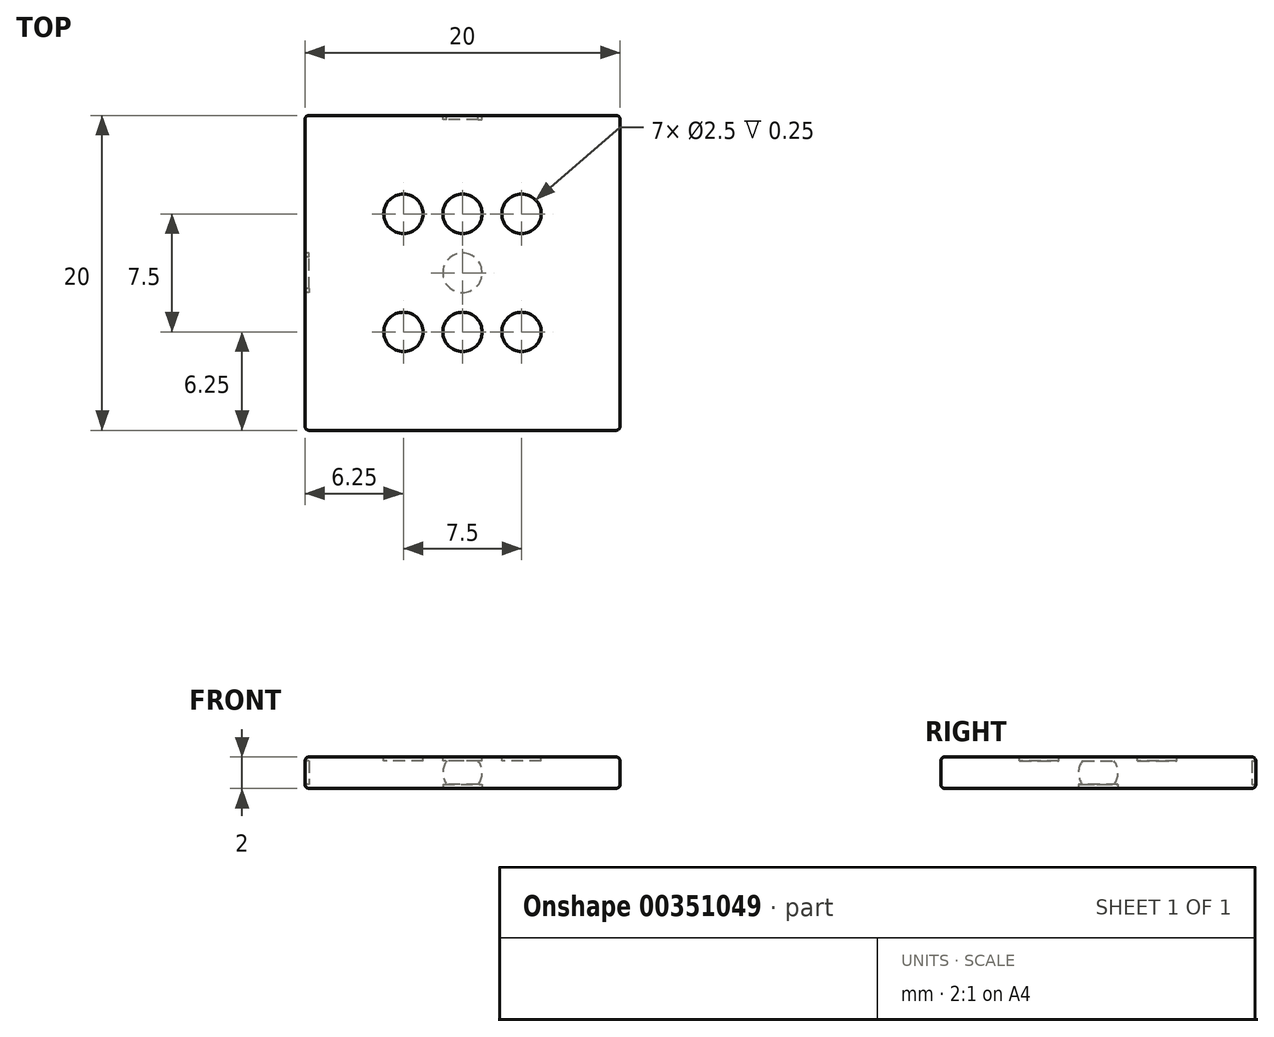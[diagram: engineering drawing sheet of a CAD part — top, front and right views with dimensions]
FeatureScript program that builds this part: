
annotation { "Feature Type Name" : "Feature", "Feature Type Description" : "" }
export const myFeature = defineFeature(function(context is Context, id is Id, definition is map)
    precondition{}
    {
        {
            assignVariable(context, id + "F0", {"name" : "H", "anyValue" : 2});
        }
        {
            assignVariable(context, id + "F1", {"name" : "E", "anyValue" : .25});
        }
        {
            var Q0;
            Q0=qCreatedBy(makeId("Top.planeOp"),FACE);
            var sketch = newSketch(context, id + "F2", { "sketchPlane" : qUnion([Q0])});
            skLineSegment(sketch, "E0.bottom", {"start": v(0, 0) * mm, "end": v(-10, 0) * mm});
            skLineSegment(sketch, "E0.top", {"start": v(0, 10) * mm, "end": v(-10, 10) * mm});
            skLineSegment(sketch, "E0.left", {"start": v(0, 0) * mm, "end": v(0, 10) * mm});
            skLineSegment(sketch, "E0.right", {"start": v(-10, 0) * mm, "end": v(-10, 10) * mm});
            skLineSegment(sketch, "E1.MirrorCS", {"start": v(0, 10) * mm, "end": v(10, 10) * mm});
            skLineSegment(sketch, "E2.MirrorCS", {"start": v(10, 0) * mm, "end": v(10, 10) * mm});
            skLineSegment(sketch, "E3.MirrorCS", {"start": v(0, 0) * mm, "end": v(10, 0) * mm});
            skLineSegment(sketch, "E4.MirrorCS", {"start": v(0, -10) * mm, "end": v(-10, -10) * mm});
            skLineSegment(sketch, "E5.MirrorCS", {"start": v(0, -10) * mm, "end": v(10, -10) * mm});
            skLineSegment(sketch, "E6.MirrorCS", {"start": v(-10, 0) * mm, "end": v(-10, -10) * mm});
            skLineSegment(sketch, "E7.MirrorCS", {"start": v(10, 0) * mm, "end": v(10, -10) * mm});
            skLineSegment(sketch, "E8", {"start": v(10, 0) * mm, "end": v(30, 0) * mm});
            skPoint(sketch, "E9", {"position": v(10, 5) * mm});
            skPoint(sketch, "E10", {"position": v(10, -5) * mm});
            skPoint(sketch, "E11", {"position": v(20, 0) * mm});
            skPoint(sketch, "E12", {"position": v(25, 0) * mm});
            skCircle(sketch, "E13", {"center": v(25, 0) * mm, "radius": 5 * mm});
            skLineSegment(sketch, "E14", {"start": v(25, 0) * mm, "end": v(10, 5) * mm});
            skLineSegment(sketch, "E15", {"start": v(10, -5) * mm, "end": v(25, 0) * mm});
            skLineSegment(sketch, "E16", {"start": v(30, 0) * mm, "end": v(10, 10) * mm});
            skLineSegment(sketch, "E17", {"start": v(30, 0) * mm, "end": v(10, -10) * mm});
            skCircle(sketch, "E18.MirrorC", {"center": v(-25, 0) * mm, "radius": 5 * mm});
            skLineSegment(sketch, "E19.MirrorCS", {"start": v(-25, 0) * mm, "end": v(-10, 5) * mm});
            skLineSegment(sketch, "E20.MirrorCS", {"start": v(-30, 0) * mm, "end": v(-10, 10) * mm});
            skLineSegment(sketch, "E21.MirrorCS", {"start": v(-10, 0) * mm, "end": v(-30, 0) * mm});
            skPoint(sketch, "E22", {"position": v(10, 7.5) * mm});
            skPoint(sketch, "E23", {"position": v(10, -7.5) * mm});
            skPoint(sketch, "E24.oppositeSnap0", {"position": v(17.5, 2.5) * mm});
            skLineSegment(sketch, "E24.bottom", {"start": v(10, 7.5) * mm, "end": v(17.5, 7.5) * mm});
            skLineSegment(sketch, "E24.top", {"start": v(10, -7.5) * mm, "end": v(17.5, -7.5) * mm});
            skLineSegment(sketch, "E24.left", {"start": v(10, 7.5) * mm, "end": v(10, -7.5) * mm});
            skLineSegment(sketch, "E24.right", {"start": v(17.5, 7.5) * mm, "end": v(17.5, -7.5) * mm});
            skLineSegment(sketch, "E25.MirrorCS", {"start": v(-10, 7.5) * mm, "end": v(-17.5, 7.5) * mm});
            skLineSegment(sketch, "E26.MirrorCS", {"start": v(-17.5, 7.5) * mm, "end": v(-17.5, -7.5) * mm});
            skLineSegment(sketch, "E27", {"start": v(13.75, 7.5) * mm, "end": v(13.75, -7.5) * mm});
            skLineSegment(sketch, "E28.MirrorCS", {"start": v(-13.75, 7.5) * mm, "end": v(-13.75, -7.5) * mm});
            skSolve(sketch);
        }
        {
            var Q0;
            Q0=makeQuery(id+"F2.imprint","IMPRINT",FACE,{"disambiguationData":[TD([[makeQuery(id+"F2.imprint","IMPRINT",EDGE,{"derivedFrom":sQuery(id+"F2.wireOp",EDGE,"E0.bottom")}),-1.0]])]});
            var Q1;
            Q1=makeQuery(id+"F2.imprint","IMPRINT",FACE,{"disambiguationData":[TD([[makeQuery(id+"F2.imprint","IMPRINT",EDGE,{"derivedFrom":sQuery(id+"F2.wireOp",EDGE,"E0.left")}),-1.0]])]});
            var Q2;
            Q2=makeQuery(id+"F2.imprint","IMPRINT",FACE,{"disambiguationData":[TD([[makeQuery(id+"F2.imprint","IMPRINT",EDGE,{"derivedFrom":sQuery(id+"F2.wireOp",EDGE,"E0.bottom")}),1.0]])]});
            extrude(context, id + "F3", {"entities" : qUnion([Q0, Q1, Q2]), "depth" : (getVariable(context, 'H') / 2) * mm, "hasSecondDirection" : true, "secondDirectionOppositeDirection" : true, "secondDirectionDepth" : (getVariable(context, 'H') / 2) * mm});
        }
        {
            var Q0;
            Q0=makeQuery(id+"F3.opExtrude","CAP_EDGE",EDGE,{"disambiguationData":[OSD([sQuery(id+"F2.wireOp",EDGE,"E4.MirrorCS"),sQuery(id+"F2.wireOp",EDGE,"E5.MirrorCS")])],"isStart":false});
            var Q1;
            Q1=makeQuery(id+"F3.opExtrude","CAP_EDGE",EDGE,{"disambiguationData":[OSD([sQuery(id+"F2.wireOp",EDGE,"E0.top"),sQuery(id+"F2.wireOp",EDGE,"E1.MirrorCS")])],"isStart":false});
            var Q2;
            Q2=makeQuery(id+"F3.opExtrude","CAP_EDGE",EDGE,{"disambiguationData":[OSD([sQuery(id+"F2.wireOp",EDGE,"E4.MirrorCS"),sQuery(id+"F2.wireOp",EDGE,"E5.MirrorCS")])],"isStart":true});
            var Q3;
            Q3=makeQuery(id+"F3.opExtrude","CAP_EDGE",EDGE,{"disambiguationData":[OSD([sQuery(id+"F2.wireOp",EDGE,"E0.top"),sQuery(id+"F2.wireOp",EDGE,"E1.MirrorCS")])],"isStart":true});
            var Q4;
            Q4=makeQuery(id+"F3.opExtrude","CAP_EDGE",EDGE,{"disambiguationData":[OSD([sQuery(id+"F2.wireOp",EDGE,"E0.right"),sQuery(id+"F2.wireOp",EDGE,"E6.MirrorCS")])],"isStart":true});
            var Q5;
            Q5=makeQuery(id+"F3.opExtrude","SWEPT_EDGE",EDGE,{"disambiguationData":[OSD([sQuery(id+"F2.wireOp",EDGE,"E0.top"),sQuery(id+"F2.wireOp",EDGE,"E0.right")])]});
            var Q6;
            Q6=makeQuery(id+"F3.opExtrude","SWEPT_FACE",FACE,{"disambiguationData":[OSD([sQuery(id+"F2.wireOp",EDGE,"E0.right"),sQuery(id+"F2.wireOp",EDGE,"E6.MirrorCS")])]});
            var Q7;
            Q7=makeQuery(id+"F3.opExtrude","SWEPT_FACE",FACE,{"disambiguationData":[OSD([sQuery(id+"F2.wireOp",EDGE,"E2.MirrorCS"),sQuery(id+"F2.wireOp",EDGE,"E7.MirrorCS")])]});
            fillet(context, id + "F4", {"entities" : qUnion([Q0, Q1, Q2, Q3, Q4, Q5, Q6, Q7]), "radius" : (getVariable(context, 'E')) * mm, "tangentPropagation" : true, "allowEdgeOverflow" : false});
        }
        {
            var Q0;
            Q0=makeQuery(id+"F3.opExtrude","CAP_FACE",FACE,{"disambiguationData":[OSD([sQuery(id+"F2.wireOp",EDGE,"E0.top"),sQuery(id+"F2.wireOp",EDGE,"E0.right"),sQuery(id+"F2.wireOp",EDGE,"E1.MirrorCS"),sQuery(id+"F2.wireOp",EDGE,"E2.MirrorCS"),sQuery(id+"F2.wireOp",EDGE,"E4.MirrorCS"),sQuery(id+"F2.wireOp",EDGE,"E5.MirrorCS"),sQuery(id+"F2.wireOp",EDGE,"E6.MirrorCS"),sQuery(id+"F2.wireOp",EDGE,"E7.MirrorCS")])],"isStart":false});
            var sketch = newSketch(context, id + "F5", { "sketchPlane" : qUnion([Q0])});
            skLineSegment(sketch, "E29.bottom", {"start": v(-3.75, 3.75) * mm, "end": v(3.75, 3.75) * mm});
            skLineSegment(sketch, "E29.top", {"start": v(-3.75, -3.75) * mm, "end": v(3.75, -3.75) * mm});
            skLineSegment(sketch, "E29.left", {"start": v(-3.75, 3.75) * mm, "end": v(-3.75, -3.75) * mm});
            skLineSegment(sketch, "E29.right", {"start": v(3.75, 3.75) * mm, "end": v(3.75, -3.75) * mm});
            skPoint(sketch, "E29.middle", {"position": v(0, 0) * mm});
            skLineSegment(sketch, "E30", {"start": v(-3.75, 0) * mm, "end": v(3.75, 0) * mm});
            skLineSegment(sketch, "E31", {"start": v(0, 3.75) * mm, "end": v(0, -3.75) * mm});
            skCircle(sketch, "E32", {"center": v(-3.75, 0) * mm, "radius": 1.25 * mm});
            skCircle(sketch, "E33", {"center": v(-3.75, 3.75) * mm, "radius": 1.25 * mm});
            skCircle(sketch, "E34", {"center": v(0, 3.75) * mm, "radius": 1.25 * mm});
            skCircle(sketch, "E35", {"center": v(0, 0) * mm, "radius": 1.25 * mm});
            skCircle(sketch, "E36.MirrorC", {"center": v(3.75, 3.75) * mm, "radius": 1.25 * mm});
            skCircle(sketch, "E37.MirrorC", {"center": v(3.75, 0) * mm, "radius": 1.25 * mm});
            skCircle(sketch, "E38.MirrorC", {"center": v(0, -3.75) * mm, "radius": 1.25 * mm});
            skCircle(sketch, "E39.MirrorC", {"center": v(-3.75, -3.75) * mm, "radius": 1.25 * mm});
            skCircle(sketch, "E40.MirrorC", {"center": v(3.75, -3.75) * mm, "radius": 1.25 * mm});
            skSolve(sketch);
        }
        {
            var Q0;
            Q0=makeQuery(id+"F3.opExtrude","CAP_FACE",FACE,{"disambiguationData":[OSD([sQuery(id+"F2.wireOp",EDGE,"E0.top"),sQuery(id+"F2.wireOp",EDGE,"E0.right"),sQuery(id+"F2.wireOp",EDGE,"E1.MirrorCS"),sQuery(id+"F2.wireOp",EDGE,"E2.MirrorCS"),sQuery(id+"F2.wireOp",EDGE,"E4.MirrorCS"),sQuery(id+"F2.wireOp",EDGE,"E5.MirrorCS"),sQuery(id+"F2.wireOp",EDGE,"E6.MirrorCS"),sQuery(id+"F2.wireOp",EDGE,"E7.MirrorCS")])],"isStart":true});
            var sketch = newSketch(context, id + "F6", { "sketchPlane" : qUnion([Q0])});
            skLineSegment(sketch, "E41.bottom", {"start": v(-3.75, 3.75) * mm, "end": v(3.75, 3.75) * mm});
            skLineSegment(sketch, "E41.top", {"start": v(-3.75, -3.75) * mm, "end": v(3.75, -3.75) * mm});
            skLineSegment(sketch, "E41.left", {"start": v(-3.75, 3.75) * mm, "end": v(-3.75, -3.75) * mm});
            skLineSegment(sketch, "E41.right", {"start": v(3.75, 3.75) * mm, "end": v(3.75, -3.75) * mm});
            skPoint(sketch, "E41.middle", {"position": v(0, 0) * mm});
            skLineSegment(sketch, "E42", {"start": v(-3.75, 0) * mm, "end": v(3.75, 0) * mm});
            skLineSegment(sketch, "E43", {"start": v(0, 3.75) * mm, "end": v(0, -3.75) * mm});
            skCircle(sketch, "E44", {"center": v(-3.75, 0) * mm, "radius": 1.25 * mm});
            skCircle(sketch, "E45", {"center": v(-3.75, 3.75) * mm, "radius": 1.25 * mm});
            skCircle(sketch, "E46", {"center": v(0, 3.75) * mm, "radius": 1.25 * mm});
            skCircle(sketch, "E47", {"center": v(0, 0) * mm, "radius": 1.25 * mm});
            skCircle(sketch, "E48.MirrorC", {"center": v(3.75, -3.75) * mm, "radius": 1.25 * mm});
            skCircle(sketch, "E49.MirrorC", {"center": v(3.75, 0) * mm, "radius": 1.25 * mm});
            skCircle(sketch, "E50.MirrorC", {"center": v(0, -3.75) * mm, "radius": 1.25 * mm});
            skCircle(sketch, "E51.MirrorC", {"center": v(-3.75, -3.75) * mm, "radius": 1.25 * mm});
            skCircle(sketch, "E52.MirrorC", {"center": v(3.75, 3.75) * mm, "radius": 1.25 * mm});
            skSolve(sketch);
        }
        {
            var Q0;
            Q0=makeQuery(id+"F3.opExtrude","SWEPT_FACE",FACE,{"disambiguationData":[OSD([sQuery(id+"F2.wireOp",EDGE,"E4.MirrorCS"),sQuery(id+"F2.wireOp",EDGE,"E5.MirrorCS")])]});
            var sketch = newSketch(context, id + "F7", { "sketchPlane" : qUnion([Q0])});
            skLineSegment(sketch, "E53.bottom", {"start": v(-3.75, 3.75) * mm, "end": v(3.75, 3.75) * mm});
            skLineSegment(sketch, "E53.top", {"start": v(-3.75, -3.75) * mm, "end": v(3.75, -3.75) * mm});
            skLineSegment(sketch, "E53.left", {"start": v(-3.75, 3.75) * mm, "end": v(-3.75, -3.75) * mm});
            skLineSegment(sketch, "E53.right", {"start": v(3.75, 3.75) * mm, "end": v(3.75, -3.75) * mm});
            skPoint(sketch, "E53.middle", {"position": v(0, 0) * mm});
            skLineSegment(sketch, "E54", {"start": v(-3.75, 0) * mm, "end": v(3.75, 0) * mm});
            skLineSegment(sketch, "E55", {"start": v(0, 3.75) * mm, "end": v(0, -3.75) * mm});
            skCircle(sketch, "E56", {"center": v(-3.75, 0) * mm, "radius": 1.25 * mm});
            skCircle(sketch, "E57", {"center": v(-3.75, 3.75) * mm, "radius": 1.25 * mm});
            skCircle(sketch, "E58", {"center": v(0, 3.75) * mm, "radius": 1.25 * mm});
            skCircle(sketch, "E59", {"center": v(0, 0) * mm, "radius": 1.25 * mm});
            skCircle(sketch, "E60.MirrorC", {"center": v(3.75, 3.75) * mm, "radius": 1.25 * mm});
            skCircle(sketch, "E61.MirrorC", {"center": v(3.75, 0) * mm, "radius": 1.25 * mm});
            skCircle(sketch, "E62.MirrorC", {"center": v(0, -3.75) * mm, "radius": 1.25 * mm});
            skCircle(sketch, "E63.MirrorC", {"center": v(-3.75, -3.75) * mm, "radius": 1.25 * mm});
            skCircle(sketch, "E64.MirrorC", {"center": v(3.75, -3.75) * mm, "radius": 1.25 * mm});
            skSolve(sketch);
        }
        {
            var Q0;
            Q0=makeQuery(id+"F3.opExtrude","SWEPT_FACE",FACE,{"disambiguationData":[OSD([sQuery(id+"F2.wireOp",EDGE,"E0.top"),sQuery(id+"F2.wireOp",EDGE,"E1.MirrorCS")])]});
            var sketch = newSketch(context, id + "F8", { "sketchPlane" : qUnion([Q0])});
            skLineSegment(sketch, "E65.bottom", {"start": v(-3.75, 3.75) * mm, "end": v(3.75, 3.75) * mm});
            skLineSegment(sketch, "E65.top", {"start": v(-3.75, -3.75) * mm, "end": v(3.75, -3.75) * mm});
            skLineSegment(sketch, "E65.left", {"start": v(-3.75, 3.75) * mm, "end": v(-3.75, -3.75) * mm});
            skLineSegment(sketch, "E65.right", {"start": v(3.75, 3.75) * mm, "end": v(3.75, -3.75) * mm});
            skPoint(sketch, "E65.middle", {"position": v(0, 0) * mm});
            skLineSegment(sketch, "E66", {"start": v(-3.75, 0) * mm, "end": v(3.75, 0) * mm});
            skLineSegment(sketch, "E67", {"start": v(0, 3.75) * mm, "end": v(0, -3.75) * mm});
            skCircle(sketch, "E68", {"center": v(-3.75, 0) * mm, "radius": 1.25 * mm});
            skCircle(sketch, "E69", {"center": v(-3.75, 3.75) * mm, "radius": 1.25 * mm});
            skCircle(sketch, "E70", {"center": v(0, 3.75) * mm, "radius": 1.25 * mm});
            skCircle(sketch, "E71", {"center": v(0, 0) * mm, "radius": 1.25 * mm});
            skCircle(sketch, "E72.MirrorC", {"center": v(3.75, -3.75) * mm, "radius": 1.25 * mm});
            skCircle(sketch, "E73.MirrorC", {"center": v(3.75, 0) * mm, "radius": 1.25 * mm});
            skCircle(sketch, "E74.MirrorC", {"center": v(0, -3.75) * mm, "radius": 1.25 * mm});
            skCircle(sketch, "E75.MirrorC", {"center": v(-3.75, -3.75) * mm, "radius": 1.25 * mm});
            skCircle(sketch, "E76.MirrorC", {"center": v(3.75, 3.75) * mm, "radius": 1.25 * mm});
            skSolve(sketch);
        }
        {
            var Q0;
            Q0=makeQuery(id+"F3.opExtrude","SWEPT_FACE",FACE,{"disambiguationData":[OSD([sQuery(id+"F2.wireOp",EDGE,"E2.MirrorCS"),sQuery(id+"F2.wireOp",EDGE,"E7.MirrorCS"),sQuery(id+"F2.wireOp",EDGE,"E24.left")])]});
            var sketch = newSketch(context, id + "F9", { "sketchPlane" : qUnion([Q0])});
            skLineSegment(sketch, "E77.bottom", {"start": v(-3.75, 3.75) * mm, "end": v(3.75, 3.75) * mm});
            skLineSegment(sketch, "E77.top", {"start": v(-3.75, -3.75) * mm, "end": v(3.75, -3.75) * mm});
            skLineSegment(sketch, "E77.left", {"start": v(-3.75, 3.75) * mm, "end": v(-3.75, -3.75) * mm});
            skLineSegment(sketch, "E77.right", {"start": v(3.75, 3.75) * mm, "end": v(3.75, -3.75) * mm});
            skPoint(sketch, "E77.middle", {"position": v(0, 0) * mm});
            skLineSegment(sketch, "E78", {"start": v(-3.75, 0) * mm, "end": v(3.75, 0) * mm});
            skLineSegment(sketch, "E79", {"start": v(0, 3.75) * mm, "end": v(0, -3.75) * mm});
            skCircle(sketch, "E80", {"center": v(-3.75, 0) * mm, "radius": 1.25 * mm});
            skCircle(sketch, "E81", {"center": v(-3.75, 3.75) * mm, "radius": 1.25 * mm});
            skCircle(sketch, "E82", {"center": v(0, 3.75) * mm, "radius": 1.25 * mm});
            skCircle(sketch, "E83", {"center": v(0, 0) * mm, "radius": 1.25 * mm});
            skCircle(sketch, "E84.MirrorC", {"center": v(3.75, -3.75) * mm, "radius": 1.25 * mm});
            skCircle(sketch, "E85.MirrorC", {"center": v(3.75, 0) * mm, "radius": 1.25 * mm});
            skCircle(sketch, "E86.MirrorC", {"center": v(0, -3.75) * mm, "radius": 1.25 * mm});
            skCircle(sketch, "E87.MirrorC", {"center": v(-3.75, -3.75) * mm, "radius": 1.25 * mm});
            skCircle(sketch, "E88.MirrorC", {"center": v(3.75, 3.75) * mm, "radius": 1.25 * mm});
            skSolve(sketch);
        }
        {
            var Q0;
            Q0=makeQuery(id+"F3.opExtrude","SWEPT_FACE",FACE,{"disambiguationData":[OSD([sQuery(id+"F2.wireOp",EDGE,"E0.right"),sQuery(id+"F2.wireOp",EDGE,"E6.MirrorCS")])]});
            var sketch = newSketch(context, id + "F10", { "sketchPlane" : qUnion([Q0])});
            skLineSegment(sketch, "E89.bottom", {"start": v(-3.75, 3.75) * mm, "end": v(3.75, 3.75) * mm});
            skLineSegment(sketch, "E89.top", {"start": v(-3.75, -3.75) * mm, "end": v(3.75, -3.75) * mm});
            skLineSegment(sketch, "E89.left", {"start": v(-3.75, 3.75) * mm, "end": v(-3.75, -3.75) * mm});
            skLineSegment(sketch, "E89.right", {"start": v(3.75, 3.75) * mm, "end": v(3.75, -3.75) * mm});
            skPoint(sketch, "E89.middle", {"position": v(0, 0) * mm});
            skLineSegment(sketch, "E90", {"start": v(-3.75, 0) * mm, "end": v(3.75, 0) * mm});
            skLineSegment(sketch, "E91", {"start": v(0, 3.75) * mm, "end": v(0, -3.75) * mm});
            skCircle(sketch, "E92", {"center": v(-3.75, 0) * mm, "radius": 1.25 * mm});
            skCircle(sketch, "E93", {"center": v(-3.75, 3.75) * mm, "radius": 1.25 * mm});
            skCircle(sketch, "E94", {"center": v(0, 3.75) * mm, "radius": 1.25 * mm});
            skCircle(sketch, "E95", {"center": v(0, 0) * mm, "radius": 1.25 * mm});
            skCircle(sketch, "E96.MirrorC", {"center": v(3.75, -3.75) * mm, "radius": 1.25 * mm});
            skCircle(sketch, "E97.MirrorC", {"center": v(3.75, 0) * mm, "radius": 1.25 * mm});
            skCircle(sketch, "E98.MirrorC", {"center": v(0, -3.75) * mm, "radius": 1.25 * mm});
            skCircle(sketch, "E99.MirrorC", {"center": v(-3.75, -3.75) * mm, "radius": 1.25 * mm});
            skCircle(sketch, "E100.MirrorC", {"center": v(3.75, 3.75) * mm, "radius": 1.25 * mm});
            skSolve(sketch);
        }
        {
            var Q0;
            {var subQ0=sQuery(id+"F5.wireOp",EDGE,"E29.bottom");var subQ1=makeQuery(id+"F5.imprint","INTERSECT",VERTEX,{"derivedFrom":[subQ0,sQuery(id+"F5.wireOp",EDGE,"E31")]});Q0=makeQuery(id+"F5.imprint","IMPRINT",FACE,{"disambiguationData":[TD([[makeQuery(id+"F5.imprint","IMPRINT",EDGE,{"disambiguationData":[TD([[subQ1,1.0]])],"derivedFrom":subQ0}),1.0]])]});}
            var Q1;
            {var subQ0=sQuery(id+"F5.wireOp",EDGE,"E31");var subQ1=sQuery(id+"F5.wireOp",EDGE,"E29.bottom");var subQ2=makeQuery(id+"F5.imprint","INTERSECT",VERTEX,{"derivedFrom":[subQ1,subQ0]});Q1=makeQuery(id+"F5.imprint","IMPRINT",FACE,{"disambiguationData":[TD([[makeQuery(id+"F5.imprint","IMPRINT",EDGE,{"disambiguationData":[TD([[subQ2,-1.0]])],"derivedFrom":subQ1}),-1.0]])]});}
            var Q2;
            {var subQ0=sQuery(id+"F5.wireOp",EDGE,"E31");var subQ1=sQuery(id+"F5.wireOp",EDGE,"E29.bottom");var subQ2=makeQuery(id+"F5.imprint","INTERSECT",VERTEX,{"derivedFrom":[subQ1,subQ0]});Q2=makeQuery(id+"F5.imprint","IMPRINT",FACE,{"disambiguationData":[TD([[makeQuery(id+"F5.imprint","IMPRINT",EDGE,{"disambiguationData":[TD([[subQ2,1.0]])],"derivedFrom":subQ1}),-1.0]])]});}
            var Q3;
            {var subQ0=sQuery(id+"F5.wireOp",EDGE,"E31");var subQ1=sQuery(id+"F5.wireOp",EDGE,"E29.top");var subQ2=makeQuery(id+"F5.imprint","INTERSECT",VERTEX,{"derivedFrom":[subQ1,subQ0]});Q3=makeQuery(id+"F5.imprint","IMPRINT",FACE,{"disambiguationData":[TD([[makeQuery(id+"F5.imprint","IMPRINT",EDGE,{"disambiguationData":[TD([[subQ2,-1.0]])],"derivedFrom":subQ1}),1.0]])]});}
            var Q4;
            {var subQ0=sQuery(id+"F5.wireOp",EDGE,"E31");var subQ1=sQuery(id+"F5.wireOp",EDGE,"E29.top");var subQ2=makeQuery(id+"F5.imprint","INTERSECT",VERTEX,{"derivedFrom":[subQ1,subQ0]});Q4=makeQuery(id+"F5.imprint","IMPRINT",FACE,{"disambiguationData":[TD([[makeQuery(id+"F5.imprint","IMPRINT",EDGE,{"disambiguationData":[TD([[subQ2,1.0]])],"derivedFrom":subQ1}),1.0]])]});}
            var Q5;
            {var subQ0=sQuery(id+"F5.wireOp",EDGE,"E29.top");var subQ1=makeQuery(id+"F5.imprint","INTERSECT",VERTEX,{"derivedFrom":[subQ0,sQuery(id+"F5.wireOp",EDGE,"E31")]});Q5=makeQuery(id+"F5.imprint","IMPRINT",FACE,{"disambiguationData":[TD([[makeQuery(id+"F5.imprint","IMPRINT",EDGE,{"disambiguationData":[TD([[subQ1,1.0]])],"derivedFrom":subQ0}),-1.0]])]});}
            var Q6;
            {var subQ0=sQuery(id+"F5.wireOp",EDGE,"E29.right");var subQ1=sQuery(id+"F5.wireOp",EDGE,"E29.bottom");var subQ2=makeQuery(id+"F5.imprint","INTERSECT",VERTEX,{"derivedFrom":[subQ1,subQ0]});Q6=makeQuery(id+"F5.imprint","IMPRINT",FACE,{"disambiguationData":[TD([[makeQuery(id+"F5.imprint","IMPRINT",EDGE,{"disambiguationData":[TD([[subQ2,1.0]])],"derivedFrom":subQ1}),1.0]])]});}
            var Q7;
            {var subQ0=sQuery(id+"F5.wireOp",EDGE,"E29.right");var subQ1=sQuery(id+"F5.wireOp",EDGE,"E29.top");var subQ2=makeQuery(id+"F5.imprint","INTERSECT",VERTEX,{"derivedFrom":[subQ1,subQ0]});Q7=makeQuery(id+"F5.imprint","IMPRINT",FACE,{"disambiguationData":[TD([[makeQuery(id+"F5.imprint","IMPRINT",EDGE,{"disambiguationData":[TD([[subQ2,1.0]])],"derivedFrom":subQ1}),-1.0]])]});}
            var Q8;
            {var subQ0=sQuery(id+"F5.wireOp",EDGE,"E29.right");var subQ1=sQuery(id+"F5.wireOp",EDGE,"E29.top");var subQ2=makeQuery(id+"F5.imprint","INTERSECT",VERTEX,{"derivedFrom":[subQ1,subQ0]});Q8=makeQuery(id+"F5.imprint","IMPRINT",FACE,{"disambiguationData":[TD([[makeQuery(id+"F5.imprint","IMPRINT",EDGE,{"disambiguationData":[TD([[subQ2,1.0]])],"derivedFrom":subQ1}),1.0]])]});}
            var Q9;
            {var subQ0=sQuery(id+"F5.wireOp",EDGE,"E29.right");var subQ1=sQuery(id+"F5.wireOp",EDGE,"E29.bottom");var subQ2=makeQuery(id+"F5.imprint","INTERSECT",VERTEX,{"derivedFrom":[subQ1,subQ0]});Q9=makeQuery(id+"F5.imprint","IMPRINT",FACE,{"disambiguationData":[TD([[makeQuery(id+"F5.imprint","IMPRINT",EDGE,{"disambiguationData":[TD([[subQ2,1.0]])],"derivedFrom":subQ1}),-1.0]])]});}
            var Q10;
            {var subQ0=sQuery(id+"F5.wireOp",EDGE,"E29.left");var subQ1=sQuery(id+"F5.wireOp",EDGE,"E29.top");var subQ2=makeQuery(id+"F5.imprint","INTERSECT",VERTEX,{"derivedFrom":[subQ1,subQ0]});Q10=makeQuery(id+"F5.imprint","IMPRINT",FACE,{"disambiguationData":[TD([[makeQuery(id+"F5.imprint","IMPRINT",EDGE,{"disambiguationData":[TD([[subQ2,-1.0]])],"derivedFrom":subQ1}),-1.0]])]});}
            var Q11;
            {var subQ0=sQuery(id+"F5.wireOp",EDGE,"E29.left");var subQ1=sQuery(id+"F5.wireOp",EDGE,"E29.top");var subQ2=makeQuery(id+"F5.imprint","INTERSECT",VERTEX,{"derivedFrom":[subQ1,subQ0]});Q11=makeQuery(id+"F5.imprint","IMPRINT",FACE,{"disambiguationData":[TD([[makeQuery(id+"F5.imprint","IMPRINT",EDGE,{"disambiguationData":[TD([[subQ2,-1.0]])],"derivedFrom":subQ1}),1.0]])]});}
            var Q12;
            {var subQ0=sQuery(id+"F5.wireOp",EDGE,"E29.left");var subQ1=sQuery(id+"F5.wireOp",EDGE,"E29.bottom");var subQ2=makeQuery(id+"F5.imprint","INTERSECT",VERTEX,{"derivedFrom":[subQ1,subQ0]});Q12=makeQuery(id+"F5.imprint","IMPRINT",FACE,{"disambiguationData":[TD([[makeQuery(id+"F5.imprint","IMPRINT",EDGE,{"disambiguationData":[TD([[subQ2,-1.0]])],"derivedFrom":subQ1}),1.0]])]});}
            var Q13;
            {var subQ0=sQuery(id+"F5.wireOp",EDGE,"E29.left");var subQ1=sQuery(id+"F5.wireOp",EDGE,"E29.bottom");var subQ2=makeQuery(id+"F5.imprint","INTERSECT",VERTEX,{"derivedFrom":[subQ1,subQ0]});Q13=makeQuery(id+"F5.imprint","IMPRINT",FACE,{"disambiguationData":[TD([[makeQuery(id+"F5.imprint","IMPRINT",EDGE,{"disambiguationData":[TD([[subQ2,-1.0]])],"derivedFrom":subQ1}),-1.0]])]});}
            extrude(context, id + "F11", {"entities" : qUnion([Q0, Q1, Q2, Q3, Q4, Q5, Q6, Q7, Q8, Q9, Q10, Q11, Q12, Q13]), "operationType" : NewBodyOperationType.REMOVE, "oppositeDirection" : true, "depth" : (getVariable(context, 'E')) * mm});
        }
        {
            var Q0;
            {var subQ0=sQuery(id+"F6.wireOp",EDGE,"E47");var subQ1=sQuery(id+"F6.wireOp",EDGE,"E42");var subQ2=makeQuery(id+"F6.imprint","INTERSECT",VERTEX,{"disambiguationData":[OD(0.0)],"derivedFrom":[subQ1,subQ0]});Q0=makeQuery(id+"F6.imprint","IMPRINT",FACE,{"disambiguationData":[TD([[makeQuery(id+"F6.imprint","IMPRINT",EDGE,{"disambiguationData":[TD([[subQ2,-1.0]])],"derivedFrom":subQ1}),1.0]])]});}
            var Q1;
            {var subQ0=sQuery(id+"F6.wireOp",EDGE,"E47");var subQ1=sQuery(id+"F6.wireOp",EDGE,"E42");var subQ2=makeQuery(id+"F6.imprint","INTERSECT",VERTEX,{"disambiguationData":[OD(0.0)],"derivedFrom":[subQ1,subQ0]});Q1=makeQuery(id+"F6.imprint","IMPRINT",FACE,{"disambiguationData":[TD([[makeQuery(id+"F6.imprint","IMPRINT",EDGE,{"disambiguationData":[TD([[subQ2,-1.0]])],"derivedFrom":subQ1}),-1.0]])]});}
            var Q2;
            {var subQ0=sQuery(id+"F6.wireOp",EDGE,"E43");var subQ1=sQuery(id+"F6.wireOp",EDGE,"E42");var subQ2=makeQuery(id+"F6.imprint","INTERSECT",VERTEX,{"derivedFrom":[subQ1,subQ0]});Q2=makeQuery(id+"F6.imprint","IMPRINT",FACE,{"disambiguationData":[TD([[makeQuery(id+"F6.imprint","IMPRINT",EDGE,{"disambiguationData":[TD([[subQ2,-1.0]])],"derivedFrom":subQ1}),-1.0]])]});}
            var Q3;
            {var subQ0=sQuery(id+"F6.wireOp",EDGE,"E43");var subQ1=sQuery(id+"F6.wireOp",EDGE,"E42");var subQ2=makeQuery(id+"F6.imprint","INTERSECT",VERTEX,{"derivedFrom":[subQ1,subQ0]});Q3=makeQuery(id+"F6.imprint","IMPRINT",FACE,{"disambiguationData":[TD([[makeQuery(id+"F6.imprint","IMPRINT",EDGE,{"disambiguationData":[TD([[subQ2,-1.0]])],"derivedFrom":subQ1}),1.0]])]});}
            extrude(context, id + "F12", {"entities" : qUnion([Q0, Q1, Q2, Q3]), "operationType" : NewBodyOperationType.REMOVE, "oppositeDirection" : true, "depth" : (getVariable(context, 'E')) * mm});
        }
        {
            var Q0;
            {var subQ0=sQuery(id+"F7.wireOp",EDGE,"E53.right");var subQ1=sQuery(id+"F7.wireOp",EDGE,"E53.top");var subQ2=makeQuery(id+"F7.imprint","INTERSECT",VERTEX,{"derivedFrom":[subQ1,subQ0]});Q0=makeQuery(id+"F7.imprint","IMPRINT",FACE,{"disambiguationData":[TD([[makeQuery(id+"F7.imprint","IMPRINT",EDGE,{"disambiguationData":[TD([[subQ2,1.0]])],"derivedFrom":subQ1}),-1.0]])]});}
            var Q1;
            {var subQ0=sQuery(id+"F7.wireOp",EDGE,"E53.right");var subQ1=sQuery(id+"F7.wireOp",EDGE,"E53.top");var subQ2=makeQuery(id+"F7.imprint","INTERSECT",VERTEX,{"derivedFrom":[subQ1,subQ0]});Q1=makeQuery(id+"F7.imprint","IMPRINT",FACE,{"disambiguationData":[TD([[makeQuery(id+"F7.imprint","IMPRINT",EDGE,{"disambiguationData":[TD([[subQ2,1.0]])],"derivedFrom":subQ1}),1.0]])]});}
            var Q2;
            {var subQ0=sQuery(id+"F7.wireOp",EDGE,"E53.right");var subQ1=sQuery(id+"F7.wireOp",EDGE,"E53.bottom");var subQ2=makeQuery(id+"F7.imprint","INTERSECT",VERTEX,{"derivedFrom":[subQ1,subQ0]});Q2=makeQuery(id+"F7.imprint","IMPRINT",FACE,{"disambiguationData":[TD([[makeQuery(id+"F7.imprint","IMPRINT",EDGE,{"disambiguationData":[TD([[subQ2,1.0]])],"derivedFrom":subQ1}),1.0]])]});}
            var Q3;
            {var subQ0=sQuery(id+"F7.wireOp",EDGE,"E53.right");var subQ1=sQuery(id+"F7.wireOp",EDGE,"E53.bottom");var subQ2=makeQuery(id+"F7.imprint","INTERSECT",VERTEX,{"derivedFrom":[subQ1,subQ0]});Q3=makeQuery(id+"F7.imprint","IMPRINT",FACE,{"disambiguationData":[TD([[makeQuery(id+"F7.imprint","IMPRINT",EDGE,{"disambiguationData":[TD([[subQ2,1.0]])],"derivedFrom":subQ1}),-1.0]])]});}
            var Q4;
            {var subQ0=sQuery(id+"F7.wireOp",EDGE,"E53.left");var subQ1=sQuery(id+"F7.wireOp",EDGE,"E53.top");var subQ2=makeQuery(id+"F7.imprint","INTERSECT",VERTEX,{"derivedFrom":[subQ1,subQ0]});Q4=makeQuery(id+"F7.imprint","IMPRINT",FACE,{"disambiguationData":[TD([[makeQuery(id+"F7.imprint","IMPRINT",EDGE,{"disambiguationData":[TD([[subQ2,-1.0]])],"derivedFrom":subQ1}),-1.0]])]});}
            var Q5;
            {var subQ0=sQuery(id+"F7.wireOp",EDGE,"E53.left");var subQ1=sQuery(id+"F7.wireOp",EDGE,"E53.bottom");var subQ2=makeQuery(id+"F7.imprint","INTERSECT",VERTEX,{"derivedFrom":[subQ1,subQ0]});Q5=makeQuery(id+"F7.imprint","IMPRINT",FACE,{"disambiguationData":[TD([[makeQuery(id+"F7.imprint","IMPRINT",EDGE,{"disambiguationData":[TD([[subQ2,-1.0]])],"derivedFrom":subQ1}),1.0]])]});}
            var Q6;
            {var subQ0=sQuery(id+"F7.wireOp",EDGE,"E53.left");var subQ1=sQuery(id+"F7.wireOp",EDGE,"E53.bottom");var subQ2=makeQuery(id+"F7.imprint","INTERSECT",VERTEX,{"derivedFrom":[subQ1,subQ0]});Q6=makeQuery(id+"F7.imprint","IMPRINT",FACE,{"disambiguationData":[TD([[makeQuery(id+"F7.imprint","IMPRINT",EDGE,{"disambiguationData":[TD([[subQ2,-1.0]])],"derivedFrom":subQ1}),-1.0]])]});}
            var Q7;
            {var subQ0=sQuery(id+"F7.wireOp",EDGE,"E53.left");var subQ1=sQuery(id+"F7.wireOp",EDGE,"E53.top");var subQ2=makeQuery(id+"F7.imprint","INTERSECT",VERTEX,{"derivedFrom":[subQ1,subQ0]});Q7=makeQuery(id+"F7.imprint","IMPRINT",FACE,{"disambiguationData":[TD([[makeQuery(id+"F7.imprint","IMPRINT",EDGE,{"disambiguationData":[TD([[subQ2,-1.0]])],"derivedFrom":subQ1}),1.0]])]});}
            extrude(context, id + "F13", {"entities" : qUnion([Q0, Q1, Q2, Q3, Q4, Q5, Q6, Q7]), "operationType" : NewBodyOperationType.REMOVE, "oppositeDirection" : true, "depth" : (getVariable(context, 'E')) * mm});
        }
        {
            var Q0;
            {var subQ0=sQuery(id+"F8.wireOp",EDGE,"E65.right");var subQ1=sQuery(id+"F8.wireOp",EDGE,"E65.top");var subQ2=makeQuery(id+"F8.imprint","INTERSECT",VERTEX,{"derivedFrom":[subQ1,subQ0]});Q0=makeQuery(id+"F8.imprint","IMPRINT",FACE,{"disambiguationData":[TD([[makeQuery(id+"F8.imprint","IMPRINT",EDGE,{"disambiguationData":[TD([[subQ2,1.0]])],"derivedFrom":subQ1}),-1.0]])]});}
            var Q1;
            {var subQ0=sQuery(id+"F8.wireOp",EDGE,"E65.right");var subQ1=sQuery(id+"F8.wireOp",EDGE,"E65.top");var subQ2=makeQuery(id+"F8.imprint","INTERSECT",VERTEX,{"derivedFrom":[subQ1,subQ0]});Q1=makeQuery(id+"F8.imprint","IMPRINT",FACE,{"disambiguationData":[TD([[makeQuery(id+"F8.imprint","IMPRINT",EDGE,{"disambiguationData":[TD([[subQ2,1.0]])],"derivedFrom":subQ1}),1.0]])]});}
            var Q2;
            {var subQ0=sQuery(id+"F8.wireOp",EDGE,"E71");var subQ1=sQuery(id+"F8.wireOp",EDGE,"E66");var subQ2=makeQuery(id+"F8.imprint","INTERSECT",VERTEX,{"disambiguationData":[OD(0.0)],"derivedFrom":[subQ1,subQ0]});Q2=makeQuery(id+"F8.imprint","IMPRINT",FACE,{"disambiguationData":[TD([[makeQuery(id+"F8.imprint","IMPRINT",EDGE,{"disambiguationData":[TD([[subQ2,-1.0]])],"derivedFrom":subQ1}),1.0]])]});}
            var Q3;
            {var subQ0=sQuery(id+"F8.wireOp",EDGE,"E71");var subQ1=sQuery(id+"F8.wireOp",EDGE,"E66");var subQ2=makeQuery(id+"F8.imprint","INTERSECT",VERTEX,{"disambiguationData":[OD(0.0)],"derivedFrom":[subQ1,subQ0]});Q3=makeQuery(id+"F8.imprint","IMPRINT",FACE,{"disambiguationData":[TD([[makeQuery(id+"F8.imprint","IMPRINT",EDGE,{"disambiguationData":[TD([[subQ2,-1.0]])],"derivedFrom":subQ1}),-1.0]])]});}
            var Q4;
            {var subQ0=sQuery(id+"F8.wireOp",EDGE,"E67");var subQ1=sQuery(id+"F8.wireOp",EDGE,"E66");var subQ2=makeQuery(id+"F8.imprint","INTERSECT",VERTEX,{"derivedFrom":[subQ1,subQ0]});Q4=makeQuery(id+"F8.imprint","IMPRINT",FACE,{"disambiguationData":[TD([[makeQuery(id+"F8.imprint","IMPRINT",EDGE,{"disambiguationData":[TD([[subQ2,-1.0]])],"derivedFrom":subQ1}),-1.0]])]});}
            var Q5;
            {var subQ0=sQuery(id+"F8.wireOp",EDGE,"E67");var subQ1=sQuery(id+"F8.wireOp",EDGE,"E66");var subQ2=makeQuery(id+"F8.imprint","INTERSECT",VERTEX,{"derivedFrom":[subQ1,subQ0]});Q5=makeQuery(id+"F8.imprint","IMPRINT",FACE,{"disambiguationData":[TD([[makeQuery(id+"F8.imprint","IMPRINT",EDGE,{"disambiguationData":[TD([[subQ2,-1.0]])],"derivedFrom":subQ1}),1.0]])]});}
            var Q6;
            {var subQ0=sQuery(id+"F8.wireOp",EDGE,"E65.left");var subQ1=sQuery(id+"F8.wireOp",EDGE,"E65.bottom");var subQ2=makeQuery(id+"F8.imprint","INTERSECT",VERTEX,{"derivedFrom":[subQ1,subQ0]});Q6=makeQuery(id+"F8.imprint","IMPRINT",FACE,{"disambiguationData":[TD([[makeQuery(id+"F8.imprint","IMPRINT",EDGE,{"disambiguationData":[TD([[subQ2,-1.0]])],"derivedFrom":subQ1}),-1.0]])]});}
            var Q7;
            {var subQ0=sQuery(id+"F8.wireOp",EDGE,"E65.left");var subQ1=sQuery(id+"F8.wireOp",EDGE,"E65.bottom");var subQ2=makeQuery(id+"F8.imprint","INTERSECT",VERTEX,{"derivedFrom":[subQ1,subQ0]});Q7=makeQuery(id+"F8.imprint","IMPRINT",FACE,{"disambiguationData":[TD([[makeQuery(id+"F8.imprint","IMPRINT",EDGE,{"disambiguationData":[TD([[subQ2,-1.0]])],"derivedFrom":subQ1}),1.0]])]});}
            extrude(context, id + "F14", {"entities" : qUnion([Q0, Q1, Q2, Q3, Q4, Q5, Q6, Q7]), "operationType" : NewBodyOperationType.REMOVE, "oppositeDirection" : true, "depth" : (getVariable(context, 'E')) * mm});
        }
        {
            var Q0;
            {var subQ0=sQuery(id+"F10.wireOp",EDGE,"E89.left");var subQ1=sQuery(id+"F10.wireOp",EDGE,"E89.bottom");var subQ2=makeQuery(id+"F10.imprint","INTERSECT",VERTEX,{"derivedFrom":[subQ1,subQ0]});Q0=makeQuery(id+"F10.imprint","IMPRINT",FACE,{"disambiguationData":[TD([[makeQuery(id+"F10.imprint","IMPRINT",EDGE,{"disambiguationData":[TD([[subQ2,-1.0]])],"derivedFrom":subQ1}),1.0]])]});}
            var Q1;
            {var subQ0=sQuery(id+"F10.wireOp",EDGE,"E89.left");var subQ1=sQuery(id+"F10.wireOp",EDGE,"E89.bottom");var subQ2=makeQuery(id+"F10.imprint","INTERSECT",VERTEX,{"derivedFrom":[subQ1,subQ0]});Q1=makeQuery(id+"F10.imprint","IMPRINT",FACE,{"disambiguationData":[TD([[makeQuery(id+"F10.imprint","IMPRINT",EDGE,{"disambiguationData":[TD([[subQ2,-1.0]])],"derivedFrom":subQ1}),-1.0]])]});}
            var Q2;
            {var subQ0=sQuery(id+"F10.wireOp",EDGE,"E89.right");var subQ1=sQuery(id+"F10.wireOp",EDGE,"E89.bottom");var subQ2=makeQuery(id+"F10.imprint","INTERSECT",VERTEX,{"derivedFrom":[subQ1,subQ0]});Q2=makeQuery(id+"F10.imprint","IMPRINT",FACE,{"disambiguationData":[TD([[makeQuery(id+"F10.imprint","IMPRINT",EDGE,{"disambiguationData":[TD([[subQ2,1.0]])],"derivedFrom":subQ1}),1.0]])]});}
            var Q3;
            {var subQ0=sQuery(id+"F10.wireOp",EDGE,"E89.right");var subQ1=sQuery(id+"F10.wireOp",EDGE,"E89.bottom");var subQ2=makeQuery(id+"F10.imprint","INTERSECT",VERTEX,{"derivedFrom":[subQ1,subQ0]});Q3=makeQuery(id+"F10.imprint","IMPRINT",FACE,{"disambiguationData":[TD([[makeQuery(id+"F10.imprint","IMPRINT",EDGE,{"disambiguationData":[TD([[subQ2,1.0]])],"derivedFrom":subQ1}),-1.0]])]});}
            var Q4;
            {var subQ0=sQuery(id+"F10.wireOp",EDGE,"E91");var subQ1=sQuery(id+"F10.wireOp",EDGE,"E90");var subQ2=makeQuery(id+"F10.imprint","INTERSECT",VERTEX,{"derivedFrom":[subQ1,subQ0]});Q4=makeQuery(id+"F10.imprint","IMPRINT",FACE,{"disambiguationData":[TD([[makeQuery(id+"F10.imprint","IMPRINT",EDGE,{"disambiguationData":[TD([[subQ2,-1.0]])],"derivedFrom":subQ1}),1.0]])]});}
            var Q5;
            {var subQ0=sQuery(id+"F10.wireOp",EDGE,"E95");var subQ1=sQuery(id+"F10.wireOp",EDGE,"E90");var subQ2=makeQuery(id+"F10.imprint","INTERSECT",VERTEX,{"disambiguationData":[OD(0.0)],"derivedFrom":[subQ1,subQ0]});Q5=makeQuery(id+"F10.imprint","IMPRINT",FACE,{"disambiguationData":[TD([[makeQuery(id+"F10.imprint","IMPRINT",EDGE,{"disambiguationData":[TD([[subQ2,-1.0]])],"derivedFrom":subQ1}),1.0]])]});}
            var Q6;
            {var subQ0=sQuery(id+"F10.wireOp",EDGE,"E91");var subQ1=sQuery(id+"F10.wireOp",EDGE,"E90");var subQ2=makeQuery(id+"F10.imprint","INTERSECT",VERTEX,{"derivedFrom":[subQ1,subQ0]});Q6=makeQuery(id+"F10.imprint","IMPRINT",FACE,{"disambiguationData":[TD([[makeQuery(id+"F10.imprint","IMPRINT",EDGE,{"disambiguationData":[TD([[subQ2,-1.0]])],"derivedFrom":subQ1}),-1.0]])]});}
            var Q7;
            {var subQ0=sQuery(id+"F10.wireOp",EDGE,"E95");var subQ1=sQuery(id+"F10.wireOp",EDGE,"E90");var subQ2=makeQuery(id+"F10.imprint","INTERSECT",VERTEX,{"disambiguationData":[OD(0.0)],"derivedFrom":[subQ1,subQ0]});Q7=makeQuery(id+"F10.imprint","IMPRINT",FACE,{"disambiguationData":[TD([[makeQuery(id+"F10.imprint","IMPRINT",EDGE,{"disambiguationData":[TD([[subQ2,-1.0]])],"derivedFrom":subQ1}),-1.0]])]});}
            var Q8;
            {var subQ0=sQuery(id+"F10.wireOp",EDGE,"E89.left");var subQ1=sQuery(id+"F10.wireOp",EDGE,"E89.top");var subQ2=makeQuery(id+"F10.imprint","INTERSECT",VERTEX,{"derivedFrom":[subQ1,subQ0]});Q8=makeQuery(id+"F10.imprint","IMPRINT",FACE,{"disambiguationData":[TD([[makeQuery(id+"F10.imprint","IMPRINT",EDGE,{"disambiguationData":[TD([[subQ2,-1.0]])],"derivedFrom":subQ1}),1.0]])]});}
            var Q9;
            {var subQ0=sQuery(id+"F10.wireOp",EDGE,"E89.left");var subQ1=sQuery(id+"F10.wireOp",EDGE,"E89.top");var subQ2=makeQuery(id+"F10.imprint","INTERSECT",VERTEX,{"derivedFrom":[subQ1,subQ0]});Q9=makeQuery(id+"F10.imprint","IMPRINT",FACE,{"disambiguationData":[TD([[makeQuery(id+"F10.imprint","IMPRINT",EDGE,{"disambiguationData":[TD([[subQ2,-1.0]])],"derivedFrom":subQ1}),-1.0]])]});}
            var Q10;
            {var subQ0=sQuery(id+"F10.wireOp",EDGE,"E89.right");var subQ1=sQuery(id+"F10.wireOp",EDGE,"E89.top");var subQ2=makeQuery(id+"F10.imprint","INTERSECT",VERTEX,{"derivedFrom":[subQ1,subQ0]});Q10=makeQuery(id+"F10.imprint","IMPRINT",FACE,{"disambiguationData":[TD([[makeQuery(id+"F10.imprint","IMPRINT",EDGE,{"disambiguationData":[TD([[subQ2,1.0]])],"derivedFrom":subQ1}),-1.0]])]});}
            var Q11;
            {var subQ0=sQuery(id+"F10.wireOp",EDGE,"E89.right");var subQ1=sQuery(id+"F10.wireOp",EDGE,"E89.top");var subQ2=makeQuery(id+"F10.imprint","INTERSECT",VERTEX,{"derivedFrom":[subQ1,subQ0]});Q11=makeQuery(id+"F10.imprint","IMPRINT",FACE,{"disambiguationData":[TD([[makeQuery(id+"F10.imprint","IMPRINT",EDGE,{"disambiguationData":[TD([[subQ2,1.0]])],"derivedFrom":subQ1}),1.0]])]});}
            extrude(context, id + "F15", {"entities" : qUnion([Q0, Q1, Q2, Q3, Q4, Q5, Q6, Q7, Q8, Q9, Q10, Q11]), "operationType" : NewBodyOperationType.REMOVE, "oppositeDirection" : true, "depth" : (getVariable(context, 'E')) * mm});
        }
        {
            var Q0;
            {var subQ0=sQuery(id+"F9.wireOp",EDGE,"E77.left");var subQ1=sQuery(id+"F9.wireOp",EDGE,"E77.bottom");var subQ2=makeQuery(id+"F9.imprint","INTERSECT",VERTEX,{"derivedFrom":[subQ1,subQ0]});Q0=makeQuery(id+"F9.imprint","IMPRINT",FACE,{"disambiguationData":[TD([[makeQuery(id+"F9.imprint","IMPRINT",EDGE,{"disambiguationData":[TD([[subQ2,-1.0]])],"derivedFrom":subQ1}),1.0]])]});}
            var Q1;
            {var subQ0=sQuery(id+"F9.wireOp",EDGE,"E77.left");var subQ1=sQuery(id+"F9.wireOp",EDGE,"E77.bottom");var subQ2=makeQuery(id+"F9.imprint","INTERSECT",VERTEX,{"derivedFrom":[subQ1,subQ0]});Q1=makeQuery(id+"F9.imprint","IMPRINT",FACE,{"disambiguationData":[TD([[makeQuery(id+"F9.imprint","IMPRINT",EDGE,{"disambiguationData":[TD([[subQ2,-1.0]])],"derivedFrom":subQ1}),-1.0]])]});}
            var Q2;
            {var subQ0=sQuery(id+"F9.wireOp",EDGE,"E77.right");var subQ1=sQuery(id+"F9.wireOp",EDGE,"E77.top");var subQ2=makeQuery(id+"F9.imprint","INTERSECT",VERTEX,{"derivedFrom":[subQ1,subQ0]});Q2=makeQuery(id+"F9.imprint","IMPRINT",FACE,{"disambiguationData":[TD([[makeQuery(id+"F9.imprint","IMPRINT",EDGE,{"disambiguationData":[TD([[subQ2,1.0]])],"derivedFrom":subQ1}),-1.0]])]});}
            var Q3;
            {var subQ0=sQuery(id+"F9.wireOp",EDGE,"E77.right");var subQ1=sQuery(id+"F9.wireOp",EDGE,"E77.top");var subQ2=makeQuery(id+"F9.imprint","INTERSECT",VERTEX,{"derivedFrom":[subQ1,subQ0]});Q3=makeQuery(id+"F9.imprint","IMPRINT",FACE,{"disambiguationData":[TD([[makeQuery(id+"F9.imprint","IMPRINT",EDGE,{"disambiguationData":[TD([[subQ2,1.0]])],"derivedFrom":subQ1}),1.0]])]});}
            extrude(context, id + "F16", {"entities" : qUnion([Q0, Q1, Q2, Q3]), "operationType" : NewBodyOperationType.REMOVE, "oppositeDirection" : true, "depth" : (getVariable(context, 'E')) * mm});
        }
    });
